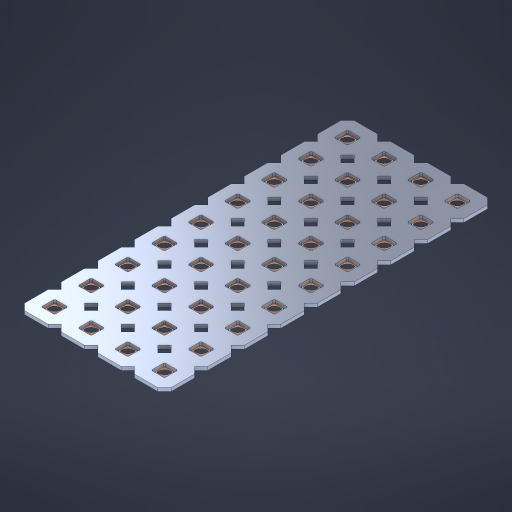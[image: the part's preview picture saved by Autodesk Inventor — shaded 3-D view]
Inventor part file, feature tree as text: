
AUTODESK INVENTOR PART (.ipt)
format: ipt  version: 2023 (Build 270158000, 158)  size: 677,888 bytes
history: native  units: in
note: dims shown in document units (in); Inventor stores cm internally (conversion verified against a paired STEP export)
features: other x37, extrude x35, sketch x2, pattern_linear x1
ambient origin geometry x8: Origin, YZ Plane, XZ Plane, XY Plane, X Axis, Y Axis, Z Axis, Center Point
bodies: Solid1 (feature_tree), Body (feature_tree)
feature tree (75):
  pattern_linear  "Rectangular Pattern1"  Spacing1=0.09in  [1 undecoded]
  sketch  "Sketch1"  dims[d1=0.5in]
  sketch  "Sketch2"  dims[d2=0.182in d3=0.09in d4=0.09in d5=0.09in d6=0.09in d7=0.09in d8=0.09in d9=0.09in d10=0.09in d11=0.02in d13=0.0in d14=0.172in d15=0.0625in d16=0.0in d19=0.5in d22=0.5in]
  other  "Srf1"
  other  "Srf126"
  other  "Srf127"
  other  "Srf128"
  other  "Srf129"
  other  "Srf130"
  other  "Srf131"
  other  "Srf250"
  other  "Srf251"
  other  "Srf268"
  other  "Srf269"
  other  "Srf270"
  other  "Srf271"
  other  "Srf272"
  other  "Srf273"
  other  "Srf274"
  other  "Srf275"
  other  "Srf276"
  other  "Srf293"
  other  "Srf294"
  other  "Srf295"
  other  "Srf296"
  other  "Srf297"
  other  "Srf298"
  other  "Srf299"
  other  "Srf300"
  other  "Srf301"
  other  "Srf318"
  other  "Srf319"
  other  "Srf320"
  other  "Srf321"
  other  "Srf322"
  other  "Srf323"
  other  "Srf324"
  other  "Srf325"
  other  "Srf326"
  other  "Circle"
  extrude  "ExtrusionSrf126"  Depth=0.09in
  extrude  "ExtrusionSrf127"  Depth=0.09in
  extrude  "ExtrusionSrf128"  Depth=0.09in
  extrude  "ExtrusionSrf129"  Depth=0.09in
  extrude  "ExtrusionSrf130"  Depth=0.09in
  extrude  "ExtrusionSrf131"  Depth=0.09in
  extrude  "ExtrusionSrf250"  Depth=0.09in
  extrude  "ExtrusionSrf251"  Depth=0.02in
  extrude  "ExtrusionSrf268"  TaperAngle=0.0deg  [1 undecoded]
  extrude  "ExtrusionSrf269"  Depth=0.5in
  extrude  "ExtrusionSrf270"  Depth=0.5in TaperAngle=0.0deg
  extrude  "ExtrusionSrf271"  Depth=0.5in
  extrude  "ExtrusionSrf272"  Depth=0.5in
  extrude  "ExtrusionSrf273"  [1 undecoded]
  extrude  "ExtrusionSrf274"  [1 undecoded]
  extrude  "ExtrusionSrf275"  [1 undecoded]
  extrude  "ExtrusionSrf276"  [1 undecoded]
  extrude  "ExtrusionSrf293"  [1 undecoded]
  extrude  "ExtrusionSrf294"  [1 undecoded]
  extrude  "ExtrusionSrf295"  [1 undecoded]
  extrude  "ExtrusionSrf296"  [1 undecoded]
  extrude  "ExtrusionSrf297"  [1 undecoded]
  extrude  "ExtrusionSrf298"  [1 undecoded]
  extrude  "ExtrusionSrf299"  [1 undecoded]
  extrude  "ExtrusionSrf300"  [1 undecoded]
  extrude  "ExtrusionSrf301"  [1 undecoded]
  extrude  "ExtrusionSrf318"  [1 undecoded]
  extrude  "ExtrusionSrf319"  [1 undecoded]
  extrude  "ExtrusionSrf320"  [1 undecoded]
  extrude  "ExtrusionSrf321"  [1 undecoded]
  extrude  "ExtrusionSrf322"  [1 undecoded]
  extrude  "ExtrusionSrf323"  [1 undecoded]
  extrude  "ExtrusionSrf324"  [1 undecoded]
  extrude  "ExtrusionSrf325"  [1 undecoded]
  extrude  "ExtrusionSrf326"  [1 undecoded]
note: 24 required parameter values undecoded (feature->parameter linkage not recoverable at this tier; creation-order binding heuristic only, values carry confidence <= 0.55)
